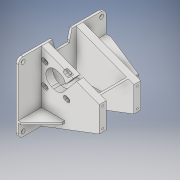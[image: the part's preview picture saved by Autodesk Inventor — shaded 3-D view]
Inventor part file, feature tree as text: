
AUTODESK INVENTOR PART (.ipt)
format: ipt  version: 2019.3 (Build 233278000, 278)  size: 457,216 bytes
history: native  units: mm
features: extrude x16, sketch x15, chamfer x7, projected_geometry x4, other x3, fillet x1, reference x1
ambient origin geometry x8: Origin, YZ Plane, XZ Plane, XY Plane, X Axis, Y Axis, Z Axis, Center Point
bodies: Solid1 (feature_tree)
feature tree (47):
  extrude  "Extrusion1"  Depth=27.5mm
  extrude  "Extrusion2"  Depth=150.0mm
  extrude  "Extrusion3"  Depth=15.0mm TaperAngle=0.0deg
  extrude  "Extrusion4"  Depth=75.0mm TaperAngle=0.0deg
  extrude  "Extrusion5"  Depth=15.0mm
  extrude  "Extrusion6"  Depth=31.75mm
  extrude  "Extrusion7"  Depth=25.0mm TaperAngle=0.0deg
  extrude  "Extrusion8"  Depth=50.0mm TaperAngle=0.0deg
  extrude  "Extrusion9"  Depth=9.0mm
  chamfer  "Chamfer3"  Distance=10.0mm
  chamfer  "Chamfer4"  Distance=10.0mm
  fillet  "Fillet1"  Radius=10.0mm
  chamfer  "Chamfer5"  Distance=10.0mm
  chamfer  "Chamfer6"  Distance=50.0mm
  extrude  "Extrusion10"  Depth=110.0mm TaperAngle=0.0deg
  extrude  "Extrusion11"  Depth=100.0mm TaperAngle=45.0deg
  extrude  "Extrusion12"  Depth=100.0mm TaperAngle=45.0deg
  chamfer  "Chamfer7"  Distance=10.0mm
  chamfer  "Chamfer8"  Distance=100.0mm Angle=15.0deg
  extrude  "Extrusion13"  Depth=100.0mm TaperAngle=15.0deg
  extrude  "Extrusion14"  Depth=2.0mm
  extrude  "Extrusion15"  Depth=2.0mm
  extrude  "Extrusion16"  Depth=2.0mm
  chamfer  "Chamfer9"  Distance=7.5mm
  sketch  "Sketch1"  dims[d0=55.0mm d1=27.5mm]
  reference  "Reference1"
  sketch  "Sketch2"  dims[d2=14.0mm d3=150.0mm]
  projected_geometry  "Projected Loop1"
  sketch  "Sketch3"  dims[d4=125.0mm d5=15.0mm d6=0.0mm]
  projected_geometry  "Projected Loop2"
  sketch  "Sketch4"  dims[d7=5.0mm d8=0.0mm d9=75.0mm d10=0.0mm]
  projected_geometry  "Projected Loop3"
  sketch  "Sketch5"  dims[d11=15.0mm d12=15.0mm]
  sketch  "Sketch6"  dims[d13=80.0mm d14=0.0mm d15=31.75mm]
  projected_geometry  "Projected Loop4"
  sketch  "Sketch7"  dims[d16=29.125mm d17=25.0mm d18=0.0mm]
  sketch  "Sketch8"  dims[d19=50.0mm d20=0.0mm d21=50.0mm d22=0.0mm]
  sketch  "Sketch9"  dims[d23=9.0mm d24=9.0mm]
  sketch  "Sketch10"  dims[d25=9.0mm]
  sketch  "Sketch12"  dims[d26=9.0mm]
  sketch  "Sketch13"  dims[d27=10.0mm]
  sketch  "Sketch15"  dims[d28=10.0mm]
  sketch  "Sketch16"  dims[d29=10.0mm]
  sketch  "Sketch17"  dims[d30=10.0mm d31=10.0mm d32=10.0mm d33=10.0mm d34=10.0mm d35=50.0mm d36=0.0mm d40=110.0mm d41=0.0mm d48=40.0mm d49=100.0mm d50=45.0deg d51=40.0mm d52=100.0mm d53=45.0deg d54=10.0mm d55=20.0mm d56=100.0mm d57=15.0deg d58=20.0mm d59=100.0mm d60=15.0deg d61=7.5mm d62=7.5mm d63=7.5mm d64=7.5mm d65=42.5mm d66=42.5mm d67=6.25mm d68=6.25mm d69=4.0mm d70=4.0mm d71=4.0mm d72=4.0mm d73=25.0mm d74=0.0mm d77=5.0mm d79=5.2mm d80=5.2mm d81=5.2mm d82=38.1mm d83=47.14mm d84=47.14mm d85=47.14mm d86=47.14mm d87=23.57mm d88=23.57mm d89=4.93mm d90=4.93mm d91=4.0mm d92=25.0mm d93=0.0mm d94=5.2mm d95=5.2mm d96=5.2mm d97=5.2mm d98=38.1mm d99=47.14mm d100=47.14mm d101=47.14mm d102=47.14mm d103=23.57mm d104=23.57mm d105=4.0mm d106=5.0mm d107=5.0mm d110=31.75mm d111=29.125mm d112=25.0mm d113=0.0mm d114=20.0mm d115=2.0mm d116=15.0deg d117=20.0mm d118=2.0mm d119=15.0deg d120=5.0mm d121=20.0mm d122=55.0mm d123=0.0mm d124=2.6mm d126=7.0mm d127=6.981317mm d128=7.0mm d131=4.5mm d132=4.5mm d133=4.5mm d134=4.5mm d135=4.5mm d136=5.0mm d137=6.0mm d138=0.0mm d139=45.0deg d140=6.0mm d141=0.0mm d142=30.0mm d143=50.0mm d144=0.0mm d145=45.0mm d146=2.0mm d147=45.0deg]
  parser-record x1  (decoder bookkeeping rows leaked as tree rows — omitted from the tree; the rows remain in map.json)
  other  "Assembly.iam"
  other  "VerticalBar:1"
note: 1 file-system path scrubbed to <path> (originals preserved in map.json)
